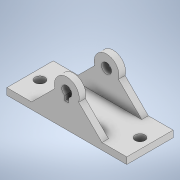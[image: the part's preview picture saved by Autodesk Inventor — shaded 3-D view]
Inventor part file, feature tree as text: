
AUTODESK INVENTOR PART (.ipt)
format: ipt  version: 2020 (Build 240168000, 168)  size: 303,616 bytes
history: native  units: mm
features: sketch x4, extrude x3, other x1, mirror x1, hole x1
ambient origin geometry x8: Origin, YZ Plane, XZ Plane, XY Plane, X Axis, Y Axis, Z Axis, Center Point
bodies: Body1 (feature_tree)
feature tree (10):
  other  "솔리드1"
  extrude  "돌출1"  Depth=30.0mm
  extrude  "돌출2"  TaperAngle=45.0deg  [1 undecoded]
  mirror  "미러1"
  hole  "구멍1"  [1 undecoded]
  extrude  "돌출3"  TaperAngle=90.0deg  [1 undecoded]
  sketch  "스케치1"
  sketch  "스케치2"
  sketch  "스케치3"
  sketch  "스케치4"
note: 3 required parameter values undecoded (feature->parameter linkage not recoverable at this tier; creation-order binding heuristic only, values carry confidence <= 0.55)
